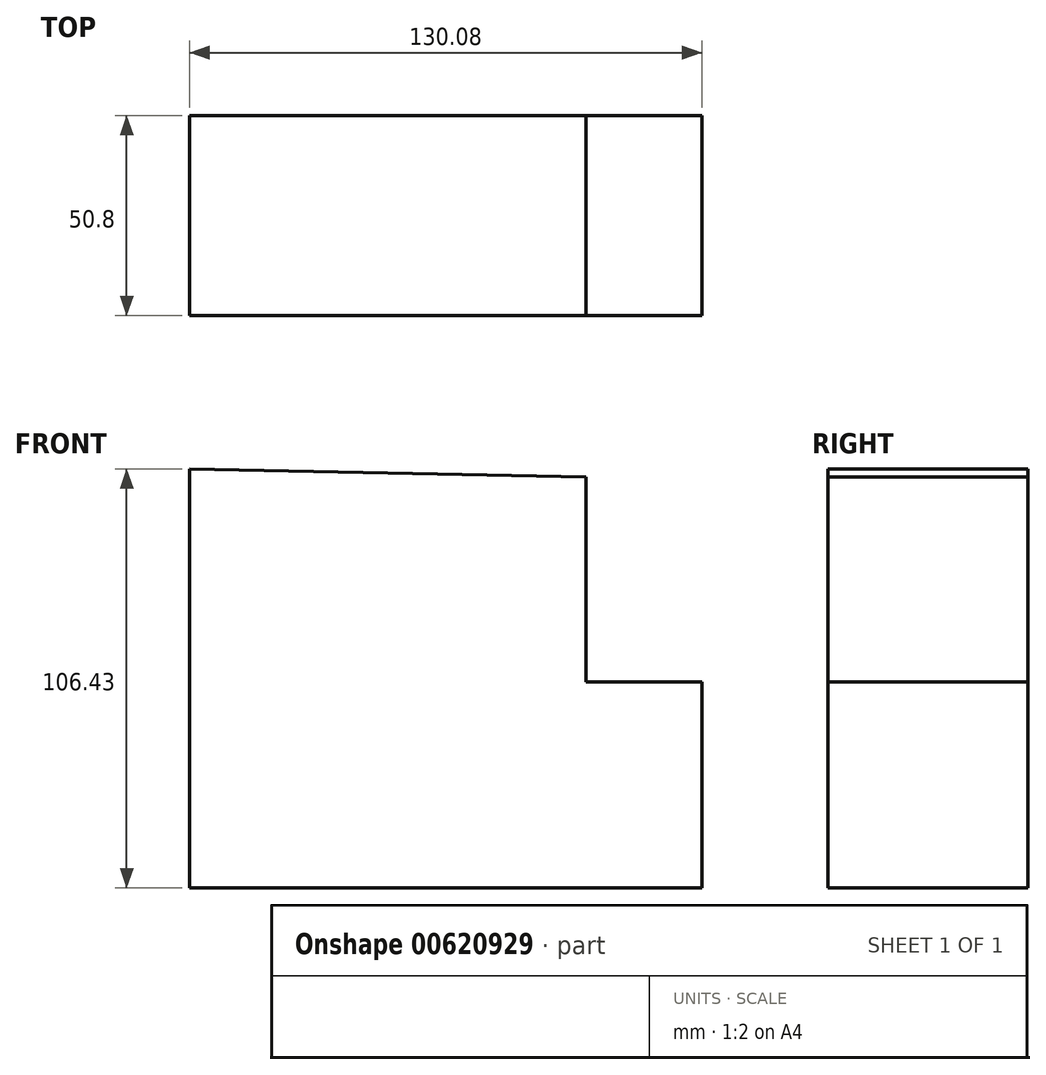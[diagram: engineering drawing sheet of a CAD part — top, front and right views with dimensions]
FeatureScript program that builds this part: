
annotation { "Feature Type Name" : "Feature", "Feature Type Description" : "" }
export const myFeature = defineFeature(function(context is Context, id is Id, definition is map)
    precondition{}
    {
        {
            var Q0;
            Q0=qCreatedBy(makeId("Front.planeOp"),FACE);
            var sketch = newSketch(context, id + "F0", { "sketchPlane" : qUnion([Q0])});
            skLineSegment(sketch, "E0", {"start": v(-69.7, 58.71) * mm, "end": v(-69.7, -47.72) * mm});
            skLineSegment(sketch, "E1", {"start": v(-69.7, -47.72) * mm, "end": v(60.37, -47.72) * mm});
            skLineSegment(sketch, "E2", {"start": v(60.37, -47.72) * mm, "end": v(60.37, 4.56) * mm});
            skLineSegment(sketch, "E3", {"start": v(60.37, 4.56) * mm, "end": v(30.91, 4.56) * mm});
            skLineSegment(sketch, "E4", {"start": v(30.91, 4.56) * mm, "end": v(30.91, 56.64) * mm});
            skLineSegment(sketch, "E5", {"start": v(30.91, 56.64) * mm, "end": v(-69.7, 58.71) * mm});
            skSolve(sketch);
        }
        {
            var Q0;
            Q0 = qSketchRegion(id + "F0", true);
            extrude(context, id + "F1", {"entities" : qUnion([Q0]), "depth" : 50.8 * mm, "offsetDistance" : 25.4 * mm});
        }
    });
